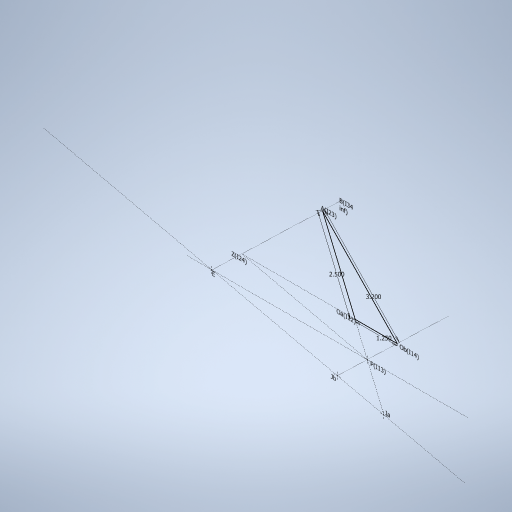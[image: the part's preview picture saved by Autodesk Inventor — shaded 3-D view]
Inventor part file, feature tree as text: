
AUTODESK INVENTOR PART (.ipt)
format: ipt  version: 2024 (Build 280153000, 153)  size: 247,808 bytes
history: native  units: in
note: dims shown in document units (in); Inventor stores cm internally (conversion verified against a paired STEP export)
features: sketch x1
ambient origin geometry x8: Origin, YZ Plane, XZ Plane, XY Plane, X Axis, Y Axis, Z Axis, Center Point
feature tree (1):
  sketch  "Sketch1"  dims[d0=1.25in d1=2.5in d2=3.2in]
